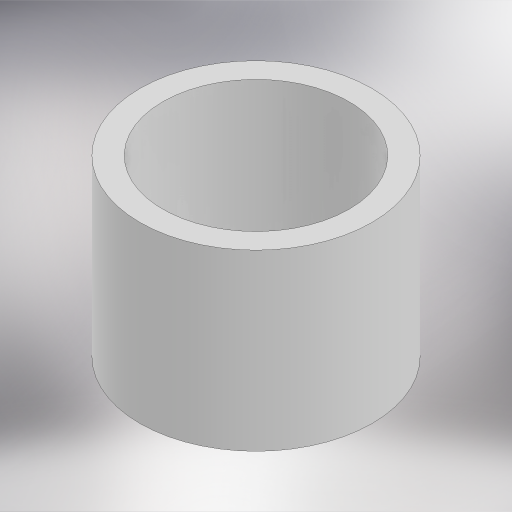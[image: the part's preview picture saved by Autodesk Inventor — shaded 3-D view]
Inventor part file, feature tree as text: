
AUTODESK INVENTOR PART (.ipt)
format: ipt  version: 2023 (Build 270158000, 158)  size: 234,496 bytes
history: native  units: in
note: dims shown in document units (in); Inventor stores cm internally (conversion verified against a paired STEP export)
features: other x1, extrude x1, sketch x1
ambient origin geometry x8: Origin, YZ Plane, XZ Plane, XY Plane, X Axis, Y Axis, Z Axis, Center Point
bodies: Body1 (feature_tree)
feature tree (3):
  other  "Sólido1"
  extrude  "Extrusión1"  Depth=0.7874in
  sketch  "Boceto2"  dims[d1=1.0492in d2=0.8425in d3=0.7874in d4=0.0in]
